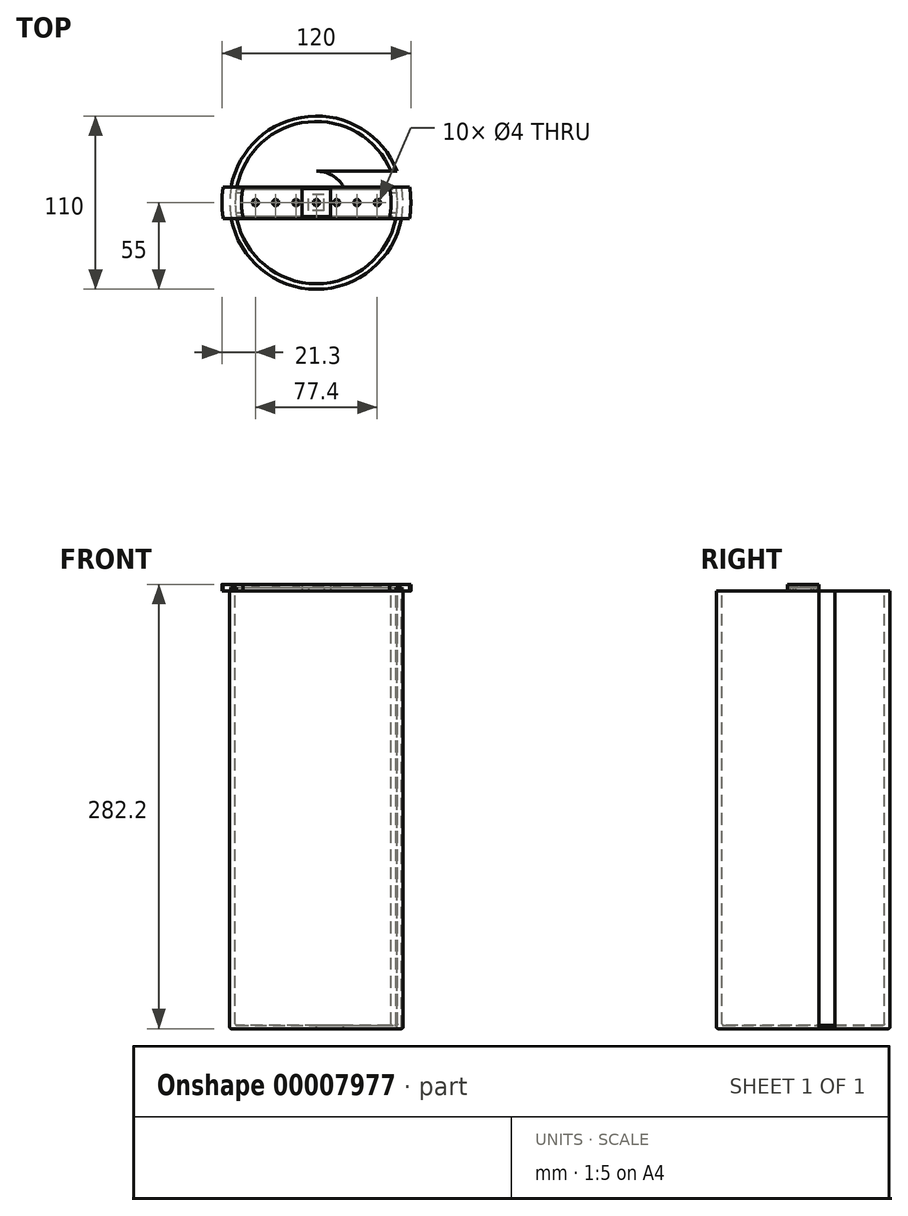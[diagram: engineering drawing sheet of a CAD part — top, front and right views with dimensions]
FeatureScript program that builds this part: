
annotation { "Feature Type Name" : "Feature", "Feature Type Description" : "" }
export const myFeature = defineFeature(function(context is Context, id is Id, definition is map)
    precondition{}
    {
        {
            var Q0;
            Q0=qCreatedBy(makeId("Top.planeOp"),FACE);
            var sketch = newSketch(context, id + "F0", { "sketchPlane" : qUnion([Q0])});
            skCircle(sketch, "E0", {"center": v(0, 0) * mm, "radius": 51.5 * mm});
            skCircle(sketch, "E1", {"center": v(0, 0) * mm, "radius": 4.8 * mm});
            skCircle(sketch, "E2", {"center": v(0, 12.6) * mm, "radius": 4.8 * mm});
            skLineSegment(sketch, "E3", {"start": v(0, 0) * mm, "end": v(0, 33.04) * mm, "construction": true});
            skCircle(sketch, "E4.1.0", {"center": v(-10.91, 6.3) * mm, "radius": 4.8 * mm});
            skCircle(sketch, "E4.2.0", {"center": v(-10.91, -6.3) * mm, "radius": 4.8 * mm});
            skCircle(sketch, "E4.3.0", {"center": v(0, -12.6) * mm, "radius": 4.8 * mm});
            skCircle(sketch, "E4.4.0", {"center": v(10.91, -6.3) * mm, "radius": 4.8 * mm});
            skCircle(sketch, "E4.5.0", {"center": v(10.91, 6.3) * mm, "radius": 4.8 * mm});
            skCircle(sketch, "E5", {"center": v(0, 0) * mm, "radius": 7.8 * mm, "construction": true});
            skCircle(sketch, "E6", {"center": v(0, 0) * mm, "radius": 20 * mm});
            skLineSegment(sketch, "E7.bottom", {"start": v(-65.9, 20) * mm, "end": v(65.9, 20) * mm});
            skLineSegment(sketch, "E7.top", {"start": v(-65.9, -20) * mm, "end": v(65.9, -20) * mm});
            skLineSegment(sketch, "E7.left", {"start": v(-65.9, 20) * mm, "end": v(-65.9, -20) * mm});
            skLineSegment(sketch, "E7.right", {"start": v(65.9, 20) * mm, "end": v(65.9, -20) * mm});
            skLineSegment(sketch, "E8", {"start": v(-65.9, 0) * mm, "end": v(65.9, 0) * mm, "construction": true});
            skCircle(sketch, "E9", {"center": v(0, 0) * mm, "radius": 55 * mm});
            skLineSegment(sketch, "E10", {"start": v(0, 20) * mm, "end": v(0, -20) * mm, "construction": true});
            skCircle(sketch, "E11", {"center": v(0, 0) * mm, "radius": 60 * mm});
            skCircle(sketch, "E12", {"center": v(0, 12.6) * mm, "radius": 1.75 * mm});
            skCircle(sketch, "E13", {"center": v(10.91, 6.3) * mm, "radius": 1.75 * mm});
            skCircle(sketch, "E14", {"center": v(10.91, -6.3) * mm, "radius": 1.75 * mm});
            skCircle(sketch, "E15", {"center": v(0, -12.6) * mm, "radius": 1.75 * mm});
            skCircle(sketch, "E16", {"center": v(-10.91, 6.3) * mm, "radius": 1.75 * mm});
            skCircle(sketch, "E17", {"center": v(-10.91, -6.3) * mm, "radius": 1.75 * mm});
            skCircle(sketch, "E18", {"center": v(0, 0) * mm, "radius": 1.75 * mm});
            skLineSegment(sketch, "E19.bottom", {"start": v(-65.9, -10) * mm, "end": v(-17.32, -10) * mm});
            skLineSegment(sketch, "E19.top", {"start": v(-65.9, 10) * mm, "end": v(-17.32, 10) * mm});
            skLineSegment(sketch, "E19.left", {"start": v(-65.9, -10) * mm, "end": v(-65.9, 10) * mm});
            skLineSegment(sketch, "E19.right", {"start": v(65.9, -10) * mm, "end": v(65.9, 10) * mm});
            skLineSegment(sketch, "E20.trimOffspring", {"start": v(17.32, -10) * mm, "end": v(65.9, -10) * mm});
            skLineSegment(sketch, "E21.trimOffspring", {"start": v(17.32, 10) * mm, "end": v(65.9, 10) * mm});
            skLineSegment(sketch, "E22.bottom", {"start": v(-24, -5) * mm, "end": v(-47.5, -5) * mm});
            skLineSegment(sketch, "E22.top", {"start": v(-24, 5) * mm, "end": v(-47.5, 5) * mm});
            skLineSegment(sketch, "E22.left", {"start": v(-24, -5) * mm, "end": v(-24, 5) * mm});
            skLineSegment(sketch, "E22.right", {"start": v(-47.5, -5) * mm, "end": v(-47.5, 5) * mm});
            skPoint(sketch, "E22.middle", {"position": v(-35.75, 0) * mm});
            skLineSegment(sketch, "E23.MirrorCS", {"start": v(24, 5) * mm, "end": v(47.5, 5) * mm});
            skLineSegment(sketch, "E24.MirrorCS", {"start": v(24, -5) * mm, "end": v(24, 5) * mm});
            skLineSegment(sketch, "E25.MirrorCS", {"start": v(24, -5) * mm, "end": v(47.5, -5) * mm});
            skLineSegment(sketch, "E26.MirrorCS", {"start": v(47.5, -5) * mm, "end": v(47.5, 5) * mm});
            skSolve(sketch);
        }
        {
            var Q0;
            {var subQ0=sQuery(id+"F0.wireOp",EDGE,"E7.bottom");var subQ1=sQuery(id+"F0.wireOp",EDGE,"E0");var subQ2=makeQuery(id+"F0.imprint","INTERSECT",VERTEX,{"disambiguationData":[OD(0.0)],"derivedFrom":[subQ1,subQ0]});Q0=makeQuery(id+"F0.imprint","IMPRINT",FACE,{"disambiguationData":[TD([[makeQuery(id+"F0.imprint","IMPRINT",EDGE,{"disambiguationData":[TD([[subQ2,-1.0]])],"derivedFrom":subQ1}),-1.0]])]});}
            var Q1;
            {var subQ0=sQuery(id+"F0.wireOp",EDGE,"E7.bottom");var subQ1=sQuery(id+"F0.wireOp",EDGE,"E0");var subQ2=makeQuery(id+"F0.imprint","INTERSECT",VERTEX,{"disambiguationData":[OD(1.0)],"derivedFrom":[subQ1,subQ0]});Q1=makeQuery(id+"F0.imprint","IMPRINT",FACE,{"disambiguationData":[TD([[makeQuery(id+"F0.imprint","IMPRINT",EDGE,{"disambiguationData":[TD([[subQ2,-1.0]])],"derivedFrom":subQ1}),-1.0]])]});}
            var Q2;
            {var subQ0=sQuery(id+"F0.wireOp",EDGE,"E19.top");var subQ1=sQuery(id+"F0.wireOp",EDGE,"E0");var subQ2=makeQuery(id+"F0.imprint","INTERSECT",VERTEX,{"derivedFrom":[subQ1,subQ0]});Q2=makeQuery(id+"F0.imprint","IMPRINT",FACE,{"disambiguationData":[TD([[makeQuery(id+"F0.imprint","IMPRINT",EDGE,{"disambiguationData":[TD([[subQ2,-1.0]])],"derivedFrom":subQ1}),-1.0]])]});}
            var Q3;
            {var subQ0=sQuery(id+"F0.wireOp",EDGE,"E19.bottom");var subQ1=sQuery(id+"F0.wireOp",EDGE,"E0");var subQ2=makeQuery(id+"F0.imprint","INTERSECT",VERTEX,{"derivedFrom":[subQ1,subQ0]});Q3=makeQuery(id+"F0.imprint","IMPRINT",FACE,{"disambiguationData":[TD([[makeQuery(id+"F0.imprint","IMPRINT",EDGE,{"disambiguationData":[TD([[subQ2,-1.0]])],"derivedFrom":subQ1}),-1.0]])]});}
            var Q4;
            {var subQ0=sQuery(id+"F0.wireOp",EDGE,"E7.top");var subQ1=sQuery(id+"F0.wireOp",EDGE,"E0");var subQ2=makeQuery(id+"F0.imprint","INTERSECT",VERTEX,{"disambiguationData":[OD(0.0)],"derivedFrom":[subQ1,subQ0]});Q4=makeQuery(id+"F0.imprint","IMPRINT",FACE,{"disambiguationData":[TD([[makeQuery(id+"F0.imprint","IMPRINT",EDGE,{"disambiguationData":[TD([[subQ2,-1.0]])],"derivedFrom":subQ1}),-1.0]])]});}
            var Q5;
            {var subQ0=sQuery(id+"F0.wireOp",EDGE,"E7.top");var subQ1=sQuery(id+"F0.wireOp",EDGE,"E0");var subQ2=makeQuery(id+"F0.imprint","INTERSECT",VERTEX,{"disambiguationData":[OD(1.0)],"derivedFrom":[subQ1,subQ0]});Q5=makeQuery(id+"F0.imprint","IMPRINT",FACE,{"disambiguationData":[TD([[makeQuery(id+"F0.imprint","IMPRINT",EDGE,{"disambiguationData":[TD([[subQ2,-1.0]])],"derivedFrom":subQ1}),-1.0]])]});}
            var Q6;
            {var subQ0=sQuery(id+"F0.wireOp",EDGE,"E21.trimOffspring");var subQ1=sQuery(id+"F0.wireOp",EDGE,"E0");var subQ2=makeQuery(id+"F0.imprint","INTERSECT",VERTEX,{"derivedFrom":[subQ1,subQ0]});Q6=makeQuery(id+"F0.imprint","IMPRINT",FACE,{"disambiguationData":[TD([[makeQuery(id+"F0.imprint","IMPRINT",EDGE,{"disambiguationData":[TD([[subQ2,1.0]])],"derivedFrom":subQ1}),-1.0]])]});}
            var Q7;
            {var subQ0=sQuery(id+"F0.wireOp",EDGE,"E7.bottom");var subQ1=sQuery(id+"F0.wireOp",EDGE,"E0");var subQ2=makeQuery(id+"F0.imprint","INTERSECT",VERTEX,{"disambiguationData":[OD(0.0)],"derivedFrom":[subQ1,subQ0]});Q7=makeQuery(id+"F0.imprint","IMPRINT",FACE,{"disambiguationData":[TD([[makeQuery(id+"F0.imprint","IMPRINT",EDGE,{"disambiguationData":[TD([[subQ2,1.0]])],"derivedFrom":subQ1}),-1.0]])]});}
            var Q8;
            {var subQ0=sQuery(id+"F0.wireOp",EDGE,"E19.top");var subQ1=sQuery(id+"F0.wireOp",EDGE,"E0");var subQ2=makeQuery(id+"F0.imprint","INTERSECT",VERTEX,{"derivedFrom":[subQ1,subQ0]});Q8=makeQuery(id+"F0.imprint","IMPRINT",FACE,{"disambiguationData":[TD([[makeQuery(id+"F0.imprint","IMPRINT",EDGE,{"disambiguationData":[TD([[subQ2,-1.0]])],"derivedFrom":subQ1}),1.0]])]});}
            var Q9;
            Q9=makeQuery(id+"F0.imprint","IMPRINT",FACE,{"disambiguationData":[TD([[makeQuery(id+"F0.imprint","IMPRINT",EDGE,{"derivedFrom":sQuery(id+"F0.wireOp",EDGE,"E4.2.0")}),1.0]])]});
            var Q10;
            {var subQ0=sQuery(id+"F0.wireOp",EDGE,"E7.bottom");var subQ1=sQuery(id+"F0.wireOp",EDGE,"E0");var subQ2=makeQuery(id+"F0.imprint","INTERSECT",VERTEX,{"disambiguationData":[OD(1.0)],"derivedFrom":[subQ1,subQ0]});Q10=makeQuery(id+"F0.imprint","IMPRINT",FACE,{"disambiguationData":[TD([[makeQuery(id+"F0.imprint","IMPRINT",EDGE,{"disambiguationData":[TD([[subQ2,-1.0]])],"derivedFrom":subQ1}),1.0]])]});}
            var Q11;
            {var subQ0=sQuery(id+"F0.wireOp",EDGE,"E7.bottom");var subQ1=sQuery(id+"F0.wireOp",EDGE,"E0");var subQ2=makeQuery(id+"F0.imprint","INTERSECT",VERTEX,{"disambiguationData":[OD(0.0)],"derivedFrom":[subQ1,subQ0]});Q11=makeQuery(id+"F0.imprint","IMPRINT",FACE,{"disambiguationData":[TD([[makeQuery(id+"F0.imprint","IMPRINT",EDGE,{"disambiguationData":[TD([[subQ2,-1.0]])],"derivedFrom":subQ1}),1.0]])]});}
            var Q12;
            {var subQ0=sQuery(id+"F0.wireOp",EDGE,"E19.bottom");var subQ1=sQuery(id+"F0.wireOp",EDGE,"E0");var subQ2=makeQuery(id+"F0.imprint","INTERSECT",VERTEX,{"derivedFrom":[subQ1,subQ0]});Q12=makeQuery(id+"F0.imprint","IMPRINT",FACE,{"disambiguationData":[TD([[makeQuery(id+"F0.imprint","IMPRINT",EDGE,{"disambiguationData":[TD([[subQ2,-1.0]])],"derivedFrom":subQ1}),1.0]])]});}
            var Q13;
            Q13=makeQuery(id+"F0.imprint","IMPRINT",FACE,{"disambiguationData":[TD([[makeQuery(id+"F0.imprint","IMPRINT",EDGE,{"derivedFrom":sQuery(id+"F0.wireOp",EDGE,"E17")}),1.0]])]});
            var Q14;
            {var subQ0=sQuery(id+"F0.wireOp",EDGE,"E7.top");var subQ1=sQuery(id+"F0.wireOp",EDGE,"E0");var subQ2=makeQuery(id+"F0.imprint","INTERSECT",VERTEX,{"disambiguationData":[OD(0.0)],"derivedFrom":[subQ1,subQ0]});Q14=makeQuery(id+"F0.imprint","IMPRINT",FACE,{"disambiguationData":[TD([[makeQuery(id+"F0.imprint","IMPRINT",EDGE,{"disambiguationData":[TD([[subQ2,-1.0]])],"derivedFrom":subQ1}),1.0]])]});}
            var Q15;
            {var subQ0=sQuery(id+"F0.wireOp",EDGE,"E7.bottom");var subQ1=sQuery(id+"F0.wireOp",EDGE,"E0");var subQ2=makeQuery(id+"F0.imprint","INTERSECT",VERTEX,{"disambiguationData":[OD(0.0)],"derivedFrom":[subQ1,subQ0]});Q15=makeQuery(id+"F0.imprint","IMPRINT",FACE,{"disambiguationData":[TD([[makeQuery(id+"F0.imprint","IMPRINT",EDGE,{"disambiguationData":[TD([[subQ2,1.0]])],"derivedFrom":subQ1}),1.0]])]});}
            var Q16;
            {var subQ0=sQuery(id+"F0.wireOp",EDGE,"E21.trimOffspring");var subQ1=sQuery(id+"F0.wireOp",EDGE,"E0");var subQ2=makeQuery(id+"F0.imprint","INTERSECT",VERTEX,{"derivedFrom":[subQ1,subQ0]});Q16=makeQuery(id+"F0.imprint","IMPRINT",FACE,{"disambiguationData":[TD([[makeQuery(id+"F0.imprint","IMPRINT",EDGE,{"disambiguationData":[TD([[subQ2,1.0]])],"derivedFrom":subQ1}),1.0]])]});}
            var Q17;
            {var subQ0=sQuery(id+"F0.wireOp",EDGE,"E7.top");var subQ1=sQuery(id+"F0.wireOp",EDGE,"E0");var subQ2=makeQuery(id+"F0.imprint","INTERSECT",VERTEX,{"disambiguationData":[OD(1.0)],"derivedFrom":[subQ1,subQ0]});Q17=makeQuery(id+"F0.imprint","IMPRINT",FACE,{"disambiguationData":[TD([[makeQuery(id+"F0.imprint","IMPRINT",EDGE,{"disambiguationData":[TD([[subQ2,-1.0]])],"derivedFrom":subQ1}),1.0]])]});}
            var Q18;
            Q18=makeQuery(id+"F0.imprint","IMPRINT",FACE,{"disambiguationData":[TD([[makeQuery(id+"F0.imprint","IMPRINT",EDGE,{"derivedFrom":sQuery(id+"F0.wireOp",EDGE,"E1")}),-1.0]])]});
            var Q19;
            Q19=makeQuery(id+"F0.imprint","IMPRINT",FACE,{"disambiguationData":[TD([[makeQuery(id+"F0.imprint","IMPRINT",EDGE,{"derivedFrom":sQuery(id+"F0.wireOp",EDGE,"E4.1.0")}),1.0]])]});
            var Q20;
            Q20=makeQuery(id+"F0.imprint","IMPRINT",FACE,{"disambiguationData":[TD([[makeQuery(id+"F0.imprint","IMPRINT",EDGE,{"derivedFrom":sQuery(id+"F0.wireOp",EDGE,"E2")}),1.0]])]});
            var Q21;
            Q21=makeQuery(id+"F0.imprint","IMPRINT",FACE,{"disambiguationData":[TD([[makeQuery(id+"F0.imprint","IMPRINT",EDGE,{"derivedFrom":sQuery(id+"F0.wireOp",EDGE,"E1")}),1.0]])]});
            var Q22;
            Q22=makeQuery(id+"F0.imprint","IMPRINT",FACE,{"disambiguationData":[TD([[makeQuery(id+"F0.imprint","IMPRINT",EDGE,{"derivedFrom":sQuery(id+"F0.wireOp",EDGE,"E4.5.0")}),1.0]])]});
            var Q23;
            Q23=makeQuery(id+"F0.imprint","IMPRINT",FACE,{"disambiguationData":[TD([[makeQuery(id+"F0.imprint","IMPRINT",EDGE,{"derivedFrom":sQuery(id+"F0.wireOp",EDGE,"E4.4.0")}),1.0]])]});
            var Q24;
            Q24=makeQuery(id+"F0.imprint","IMPRINT",FACE,{"disambiguationData":[TD([[makeQuery(id+"F0.imprint","IMPRINT",EDGE,{"derivedFrom":sQuery(id+"F0.wireOp",EDGE,"E4.3.0")}),1.0]])]});
            var Q25;
            Q25=makeQuery(id+"F0.imprint","IMPRINT",FACE,{"disambiguationData":[TD([[makeQuery(id+"F0.imprint","IMPRINT",EDGE,{"derivedFrom":sQuery(id+"F0.wireOp",EDGE,"E16")}),1.0]])]});
            var Q26;
            Q26=makeQuery(id+"F0.imprint","IMPRINT",FACE,{"disambiguationData":[TD([[makeQuery(id+"F0.imprint","IMPRINT",EDGE,{"derivedFrom":sQuery(id+"F0.wireOp",EDGE,"E12")}),1.0]])]});
            var Q27;
            Q27=makeQuery(id+"F0.imprint","IMPRINT",FACE,{"disambiguationData":[TD([[makeQuery(id+"F0.imprint","IMPRINT",EDGE,{"derivedFrom":sQuery(id+"F0.wireOp",EDGE,"E13")}),1.0]])]});
            var Q28;
            Q28=makeQuery(id+"F0.imprint","IMPRINT",FACE,{"disambiguationData":[TD([[makeQuery(id+"F0.imprint","IMPRINT",EDGE,{"derivedFrom":sQuery(id+"F0.wireOp",EDGE,"E14")}),1.0]])]});
            var Q29;
            Q29=makeQuery(id+"F0.imprint","IMPRINT",FACE,{"disambiguationData":[TD([[makeQuery(id+"F0.imprint","IMPRINT",EDGE,{"derivedFrom":sQuery(id+"F0.wireOp",EDGE,"E18")}),1.0]])]});
            var Q30;
            Q30=makeQuery(id+"F0.imprint","IMPRINT",FACE,{"disambiguationData":[TD([[makeQuery(id+"F0.imprint","IMPRINT",EDGE,{"derivedFrom":sQuery(id+"F0.wireOp",EDGE,"E15")}),1.0]])]});
            var Q31;
            Q31=makeQuery(id+"F0.imprint","IMPRINT",FACE,{"disambiguationData":[TD([[makeQuery(id+"F0.imprint","IMPRINT",EDGE,{"derivedFrom":sQuery(id+"F0.wireOp",EDGE,"E22.bottom")}),-1.0]])]});
            var Q32;
            Q32=makeQuery(id+"F0.imprint","IMPRINT",FACE,{"disambiguationData":[TD([[makeQuery(id+"F0.imprint","IMPRINT",EDGE,{"derivedFrom":sQuery(id+"F0.wireOp",EDGE,"E23.MirrorCS")}),-1.0]])]});
            extrude(context, id + "F1", {"entities" : qUnion([Q0, Q1, Q2, Q3, Q4, Q5, Q6, Q7, Q8, Q9, Q10, Q11, Q12, Q13, Q14, Q15, Q16, Q17, Q18, Q19, Q20, Q21, Q22, Q23, Q24, Q25, Q26, Q27, Q28, Q29, Q30, Q31, Q32]), "oppositeDirection" : true, "depth" : 278 * mm});
        }
        {
            var Q0;
            {var subQ0=sQuery(id+"F0.wireOp",EDGE,"E7.bottom");var subQ1=sQuery(id+"F0.wireOp",EDGE,"E0");var subQ2=makeQuery(id+"F0.imprint","INTERSECT",VERTEX,{"disambiguationData":[OD(0.0)],"derivedFrom":[subQ1,subQ0]});Q0=makeQuery(id+"F0.imprint","IMPRINT",FACE,{"disambiguationData":[TD([[makeQuery(id+"F0.imprint","IMPRINT",EDGE,{"disambiguationData":[TD([[subQ2,-1.0]])],"derivedFrom":subQ1}),1.0]])]});}
            var Q1;
            {var subQ0=sQuery(id+"F0.wireOp",EDGE,"E7.bottom");var subQ1=sQuery(id+"F0.wireOp",EDGE,"E0");var subQ2=makeQuery(id+"F0.imprint","INTERSECT",VERTEX,{"disambiguationData":[OD(0.0)],"derivedFrom":[subQ1,subQ0]});Q1=makeQuery(id+"F0.imprint","IMPRINT",FACE,{"disambiguationData":[TD([[makeQuery(id+"F0.imprint","IMPRINT",EDGE,{"disambiguationData":[TD([[subQ2,1.0]])],"derivedFrom":subQ1}),1.0]])]});}
            var Q2;
            {var subQ0=sQuery(id+"F0.wireOp",EDGE,"E21.trimOffspring");var subQ1=sQuery(id+"F0.wireOp",EDGE,"E0");var subQ2=makeQuery(id+"F0.imprint","INTERSECT",VERTEX,{"derivedFrom":[subQ1,subQ0]});Q2=makeQuery(id+"F0.imprint","IMPRINT",FACE,{"disambiguationData":[TD([[makeQuery(id+"F0.imprint","IMPRINT",EDGE,{"disambiguationData":[TD([[subQ2,1.0]])],"derivedFrom":subQ1}),1.0]])]});}
            var Q3;
            {var subQ0=sQuery(id+"F0.wireOp",EDGE,"E7.top");var subQ1=sQuery(id+"F0.wireOp",EDGE,"E0");var subQ2=makeQuery(id+"F0.imprint","INTERSECT",VERTEX,{"disambiguationData":[OD(1.0)],"derivedFrom":[subQ1,subQ0]});Q3=makeQuery(id+"F0.imprint","IMPRINT",FACE,{"disambiguationData":[TD([[makeQuery(id+"F0.imprint","IMPRINT",EDGE,{"disambiguationData":[TD([[subQ2,-1.0]])],"derivedFrom":subQ1}),1.0]])]});}
            var Q4;
            {var subQ0=sQuery(id+"F0.wireOp",EDGE,"E7.top");var subQ1=sQuery(id+"F0.wireOp",EDGE,"E0");var subQ2=makeQuery(id+"F0.imprint","INTERSECT",VERTEX,{"disambiguationData":[OD(0.0)],"derivedFrom":[subQ1,subQ0]});Q4=makeQuery(id+"F0.imprint","IMPRINT",FACE,{"disambiguationData":[TD([[makeQuery(id+"F0.imprint","IMPRINT",EDGE,{"disambiguationData":[TD([[subQ2,-1.0]])],"derivedFrom":subQ1}),1.0]])]});}
            var Q5;
            {var subQ0=sQuery(id+"F0.wireOp",EDGE,"E19.bottom");var subQ1=sQuery(id+"F0.wireOp",EDGE,"E0");var subQ2=makeQuery(id+"F0.imprint","INTERSECT",VERTEX,{"derivedFrom":[subQ1,subQ0]});Q5=makeQuery(id+"F0.imprint","IMPRINT",FACE,{"disambiguationData":[TD([[makeQuery(id+"F0.imprint","IMPRINT",EDGE,{"disambiguationData":[TD([[subQ2,-1.0]])],"derivedFrom":subQ1}),1.0]])]});}
            var Q6;
            {var subQ0=sQuery(id+"F0.wireOp",EDGE,"E7.bottom");var subQ1=sQuery(id+"F0.wireOp",EDGE,"E0");var subQ2=makeQuery(id+"F0.imprint","INTERSECT",VERTEX,{"disambiguationData":[OD(1.0)],"derivedFrom":[subQ1,subQ0]});Q6=makeQuery(id+"F0.imprint","IMPRINT",FACE,{"disambiguationData":[TD([[makeQuery(id+"F0.imprint","IMPRINT",EDGE,{"disambiguationData":[TD([[subQ2,-1.0]])],"derivedFrom":subQ1}),1.0]])]});}
            var Q7;
            {var subQ0=sQuery(id+"F0.wireOp",EDGE,"E19.top");var subQ1=sQuery(id+"F0.wireOp",EDGE,"E0");var subQ2=makeQuery(id+"F0.imprint","INTERSECT",VERTEX,{"derivedFrom":[subQ1,subQ0]});Q7=makeQuery(id+"F0.imprint","IMPRINT",FACE,{"disambiguationData":[TD([[makeQuery(id+"F0.imprint","IMPRINT",EDGE,{"disambiguationData":[TD([[subQ2,-1.0]])],"derivedFrom":subQ1}),1.0]])]});}
            var Q8;
            Q8=makeQuery(id+"F0.imprint","IMPRINT",FACE,{"disambiguationData":[TD([[makeQuery(id+"F0.imprint","IMPRINT",EDGE,{"derivedFrom":sQuery(id+"F0.wireOp",EDGE,"E1")}),-1.0]])]});
            var Q9;
            Q9=makeQuery(id+"F0.imprint","IMPRINT",FACE,{"disambiguationData":[TD([[makeQuery(id+"F0.imprint","IMPRINT",EDGE,{"derivedFrom":sQuery(id+"F0.wireOp",EDGE,"E4.4.0")}),1.0]])]});
            var Q10;
            Q10=makeQuery(id+"F0.imprint","IMPRINT",FACE,{"disambiguationData":[TD([[makeQuery(id+"F0.imprint","IMPRINT",EDGE,{"derivedFrom":sQuery(id+"F0.wireOp",EDGE,"E14")}),1.0]])]});
            var Q11;
            Q11=makeQuery(id+"F0.imprint","IMPRINT",FACE,{"disambiguationData":[TD([[makeQuery(id+"F0.imprint","IMPRINT",EDGE,{"derivedFrom":sQuery(id+"F0.wireOp",EDGE,"E13")}),1.0]])]});
            var Q12;
            Q12=makeQuery(id+"F0.imprint","IMPRINT",FACE,{"disambiguationData":[TD([[makeQuery(id+"F0.imprint","IMPRINT",EDGE,{"derivedFrom":sQuery(id+"F0.wireOp",EDGE,"E4.5.0")}),1.0]])]});
            var Q13;
            Q13=makeQuery(id+"F0.imprint","IMPRINT",FACE,{"disambiguationData":[TD([[makeQuery(id+"F0.imprint","IMPRINT",EDGE,{"derivedFrom":sQuery(id+"F0.wireOp",EDGE,"E2")}),1.0]])]});
            var Q14;
            Q14=makeQuery(id+"F0.imprint","IMPRINT",FACE,{"disambiguationData":[TD([[makeQuery(id+"F0.imprint","IMPRINT",EDGE,{"derivedFrom":sQuery(id+"F0.wireOp",EDGE,"E12")}),1.0]])]});
            var Q15;
            Q15=makeQuery(id+"F0.imprint","IMPRINT",FACE,{"disambiguationData":[TD([[makeQuery(id+"F0.imprint","IMPRINT",EDGE,{"derivedFrom":sQuery(id+"F0.wireOp",EDGE,"E4.1.0")}),1.0]])]});
            var Q16;
            Q16=makeQuery(id+"F0.imprint","IMPRINT",FACE,{"disambiguationData":[TD([[makeQuery(id+"F0.imprint","IMPRINT",EDGE,{"derivedFrom":sQuery(id+"F0.wireOp",EDGE,"E16")}),1.0]])]});
            var Q17;
            Q17=makeQuery(id+"F0.imprint","IMPRINT",FACE,{"disambiguationData":[TD([[makeQuery(id+"F0.imprint","IMPRINT",EDGE,{"derivedFrom":sQuery(id+"F0.wireOp",EDGE,"E4.2.0")}),1.0]])]});
            var Q18;
            Q18=makeQuery(id+"F0.imprint","IMPRINT",FACE,{"disambiguationData":[TD([[makeQuery(id+"F0.imprint","IMPRINT",EDGE,{"derivedFrom":sQuery(id+"F0.wireOp",EDGE,"E17")}),1.0]])]});
            var Q19;
            Q19=makeQuery(id+"F0.imprint","IMPRINT",FACE,{"disambiguationData":[TD([[makeQuery(id+"F0.imprint","IMPRINT",EDGE,{"derivedFrom":sQuery(id+"F0.wireOp",EDGE,"E4.3.0")}),1.0]])]});
            var Q20;
            Q20=makeQuery(id+"F0.imprint","IMPRINT",FACE,{"disambiguationData":[TD([[makeQuery(id+"F0.imprint","IMPRINT",EDGE,{"derivedFrom":sQuery(id+"F0.wireOp",EDGE,"E15")}),1.0]])]});
            var Q21;
            Q21=makeQuery(id+"F0.imprint","IMPRINT",FACE,{"disambiguationData":[TD([[makeQuery(id+"F0.imprint","IMPRINT",EDGE,{"derivedFrom":sQuery(id+"F0.wireOp",EDGE,"E1")}),1.0]])]});
            var Q22;
            Q22=makeQuery(id+"F0.imprint","IMPRINT",FACE,{"disambiguationData":[TD([[makeQuery(id+"F0.imprint","IMPRINT",EDGE,{"derivedFrom":sQuery(id+"F0.wireOp",EDGE,"E18")}),1.0]])]});
            var Q23;
            Q23=makeQuery(id+"F0.imprint","IMPRINT",FACE,{"disambiguationData":[TD([[makeQuery(id+"F0.imprint","IMPRINT",EDGE,{"derivedFrom":sQuery(id+"F0.wireOp",EDGE,"E22.bottom")}),-1.0]])]});
            var Q24;
            Q24=makeQuery(id+"F0.imprint","IMPRINT",FACE,{"disambiguationData":[TD([[makeQuery(id+"F0.imprint","IMPRINT",EDGE,{"derivedFrom":sQuery(id+"F0.wireOp",EDGE,"E23.MirrorCS")}),-1.0]])]});
            extrude(context, id + "F2", {"entities" : qUnion([Q0, Q1, Q2, Q3, Q4, Q5, Q6, Q7, Q8, Q9, Q10, Q11, Q12, Q13, Q14, Q15, Q16, Q17, Q18, Q19, Q20, Q21, Q22, Q23, Q24]), "operationType" : NewBodyOperationType.REMOVE, "oppositeDirection" : true, "depth" : 276 * mm});
        }
        {
            var Q0;
            Q0=makeQuery(id+"F2.boolean.opBoolean","COPY",EDGE,{"derivedFrom":makeQuery(id+"F2.opExtrude","CAP_EDGE",EDGE,{"disambiguationData":[OSD([sQuery(id+"F0.wireOp",EDGE,"E0")])],"isStart":false})});
            var Q1;
            Q1=makeQuery(id+"F1.opExtrude","CAP_EDGE",EDGE,{"disambiguationData":[OSD([sQuery(id+"F0.wireOp",EDGE,"E9")])],"isStart":false});
            fillet(context, id + "F3", {"entities" : qUnion([Q0, Q1]), "radius" : 1 * mm, "tangentPropagation" : true, "allowEdgeOverflow" : false});
        }
        {
            var Q0;
            Q0=qCreatedBy(makeId("Top.planeOp"),FACE);
            var sketch = newSketch(context, id + "F4", { "sketchPlane" : qUnion([Q0])});
            skLineSegment(sketch, "E27.0", {"start": v(-59.16, 10) * mm, "end": v(-17.32, 10) * mm});
            skLineSegment(sketch, "E27.1", {"start": v(17.32, 10) * mm, "end": v(59.16, 10) * mm});
            skLineSegment(sketch, "E27.2", {"start": v(17.32, -10) * mm, "end": v(59.16, -10) * mm});
            skLineSegment(sketch, "E27.3", {"start": v(-59.16, -10) * mm, "end": v(-17.32, -10) * mm});
            skCircle(sketch, "E27.4", {"center": v(0, 0) * mm, "radius": 60 * mm});
            skCircle(sketch, "E27.5", {"center": v(0, 0) * mm, "radius": 51.5 * mm});
            skCircle(sketch, "E27.6", {"center": v(0, 0) * mm, "radius": 55 * mm});
            skLineSegment(sketch, "E28.0", {"start": v(0, 0) * mm, "end": v(0, 33.04) * mm, "construction": true});
            skLineSegment(sketch, "E28.1", {"start": v(0, 20) * mm, "end": v(0, -20) * mm, "construction": true});
            skLineSegment(sketch, "E29", {"start": v(-17.32, 10) * mm, "end": v(17.32, 10) * mm});
            skLineSegment(sketch, "E30", {"start": v(-17.32, -10) * mm, "end": v(17.32, -10) * mm});
            skCircle(sketch, "E31", {"center": v(0, 0) * mm, "radius": 47.5 * mm});
            skLineSegment(sketch, "E32.bottom", {"start": v(4.95, -4.95) * mm, "end": v(-4.95, -4.95) * mm});
            skLineSegment(sketch, "E32.top", {"start": v(4.95, 4.95) * mm, "end": v(-4.95, 4.95) * mm});
            skLineSegment(sketch, "E32.left", {"start": v(4.95, -4.95) * mm, "end": v(4.95, 4.95) * mm});
            skLineSegment(sketch, "E32.right", {"start": v(-4.95, -4.95) * mm, "end": v(-4.95, 4.95) * mm});
            skLineSegment(sketch, "E33.1.0.0", {"start": v(17.85, 4.95) * mm, "end": v(7.95, 4.95) * mm});
            skLineSegment(sketch, "E33.1.0.1", {"start": v(17.85, -4.95) * mm, "end": v(17.85, 4.95) * mm});
            skLineSegment(sketch, "E33.1.0.2", {"start": v(17.85, -4.95) * mm, "end": v(7.95, -4.95) * mm});
            skLineSegment(sketch, "E33.1.0.3", {"start": v(7.95, -4.95) * mm, "end": v(7.95, 4.95) * mm});
            skLineSegment(sketch, "E33.2.0.0", {"start": v(30.75, 4.95) * mm, "end": v(20.85, 4.95) * mm});
            skLineSegment(sketch, "E33.2.0.1", {"start": v(30.75, -4.95) * mm, "end": v(30.75, 4.95) * mm});
            skLineSegment(sketch, "E33.2.0.2", {"start": v(30.75, -4.95) * mm, "end": v(20.85, -4.95) * mm});
            skLineSegment(sketch, "E33.2.0.3", {"start": v(20.85, -4.95) * mm, "end": v(20.85, 4.95) * mm});
            skLineSegment(sketch, "E33.3.0.0", {"start": v(43.65, 4.95) * mm, "end": v(33.75, 4.95) * mm});
            skLineSegment(sketch, "E33.3.0.1", {"start": v(43.65, -4.95) * mm, "end": v(43.65, 4.95) * mm});
            skLineSegment(sketch, "E33.3.0.2", {"start": v(43.65, -4.95) * mm, "end": v(33.75, -4.95) * mm});
            skLineSegment(sketch, "E33.3.0.3", {"start": v(33.75, -4.95) * mm, "end": v(33.75, 4.95) * mm});
            skLineSegment(sketch, "E33.direction1", {"start": v(-4.95, 4.95) * mm, "end": v(7.95, 4.95) * mm, "construction": true});
            skLineSegment(sketch, "E34.MirrorCS", {"start": v(-17.85, 4.95) * mm, "end": v(-7.95, 4.95) * mm});
            skLineSegment(sketch, "E35.MirrorCS", {"start": v(-17.85, -4.95) * mm, "end": v(-17.85, 4.95) * mm});
            skLineSegment(sketch, "E36.MirrorCS", {"start": v(-17.85, -4.95) * mm, "end": v(-7.95, -4.95) * mm});
            skLineSegment(sketch, "E37.MirrorCS", {"start": v(-7.95, -4.95) * mm, "end": v(-7.95, 4.95) * mm});
            skLineSegment(sketch, "E38.MirrorCS", {"start": v(-20.85, -4.95) * mm, "end": v(-20.85, 4.95) * mm});
            skLineSegment(sketch, "E39.MirrorCS", {"start": v(-30.75, 4.95) * mm, "end": v(-20.85, 4.95) * mm});
            skLineSegment(sketch, "E40.MirrorCS", {"start": v(-30.75, -4.95) * mm, "end": v(-20.85, -4.95) * mm});
            skLineSegment(sketch, "E41.MirrorCS", {"start": v(-30.75, -4.95) * mm, "end": v(-30.75, 4.95) * mm});
            skLineSegment(sketch, "E42.MirrorCS", {"start": v(-33.75, -4.95) * mm, "end": v(-33.75, 4.95) * mm});
            skLineSegment(sketch, "E43.MirrorCS", {"start": v(-43.65, -4.95) * mm, "end": v(-33.75, -4.95) * mm});
            skLineSegment(sketch, "E44.MirrorCS", {"start": v(-43.65, 4.95) * mm, "end": v(-33.75, 4.95) * mm});
            skLineSegment(sketch, "E45.MirrorCS", {"start": v(-43.65, -4.95) * mm, "end": v(-43.65, 4.95) * mm});
            skCircle(sketch, "E46", {"center": v(0, 0) * mm, "radius": 2 * mm});
            skCircle(sketch, "E47.1.0.0", {"center": v(12.9, 0) * mm, "radius": 2 * mm});
            skCircle(sketch, "E47.2.0.0", {"center": v(25.8, 0) * mm, "radius": 2 * mm});
            skCircle(sketch, "E47.3.0.0", {"center": v(38.7, 0) * mm, "radius": 2 * mm});
            skLineSegment(sketch, "E47.direction1", {"start": v(0, 0) * mm, "end": v(12.9, 0) * mm, "construction": true});
            skCircle(sketch, "E48.MirrorC", {"center": v(-12.9, 0) * mm, "radius": 2 * mm});
            skCircle(sketch, "E49.MirrorC", {"center": v(-25.8, 0) * mm, "radius": 2 * mm});
            skCircle(sketch, "E50.MirrorC", {"center": v(-38.7, 0) * mm, "radius": 2 * mm});
            skSolve(sketch);
        }
        {
            var Q0;
            {var subQ0=sQuery(id+"F4.wireOp",EDGE,"E29");Q0=makeQuery(id+"F4.imprint","IMPRINT",FACE,{"disambiguationData":[TD([[makeQuery(id+"F4.imprint","IMPRINT",EDGE,{"derivedFrom":subQ0}),-1.0]])]});}
            var Q1;
            {var subQ0=sQuery(id+"F4.wireOp",EDGE,"E27.5");var subQ1=sQuery(id+"F4.wireOp",EDGE,"E27.0");var subQ2=makeQuery(id+"F4.imprint","INTERSECT",VERTEX,{"derivedFrom":[subQ1,subQ0]});Q1=makeQuery(id+"F4.imprint","IMPRINT",FACE,{"disambiguationData":[TD([[makeQuery(id+"F4.imprint","IMPRINT",EDGE,{"disambiguationData":[TD([[subQ2,-1.0]])],"derivedFrom":subQ1}),-1.0]])]});}
            var Q2;
            {var subQ0=sQuery(id+"F4.wireOp",EDGE,"E27.4");var subQ1=sQuery(id+"F4.wireOp",EDGE,"E27.0");var subQ2=makeQuery(id+"F4.imprint","INTERSECT",VERTEX,{"derivedFrom":[subQ1,subQ0]});Q2=makeQuery(id+"F4.imprint","IMPRINT",FACE,{"disambiguationData":[TD([[makeQuery(id+"F4.imprint","IMPRINT",EDGE,{"disambiguationData":[TD([[subQ2,-1.0]])],"derivedFrom":subQ1}),-1.0]])]});}
            var Q3;
            {var subQ0=sQuery(id+"F4.wireOp",EDGE,"E27.6");var subQ1=sQuery(id+"F4.wireOp",EDGE,"E27.0");var subQ2=makeQuery(id+"F4.imprint","INTERSECT",VERTEX,{"derivedFrom":[subQ1,subQ0]});Q3=makeQuery(id+"F4.imprint","IMPRINT",FACE,{"disambiguationData":[TD([[makeQuery(id+"F4.imprint","IMPRINT",EDGE,{"disambiguationData":[TD([[subQ2,-1.0]])],"derivedFrom":subQ1}),-1.0]])]});}
            var Q4;
            {var subQ0=sQuery(id+"F4.wireOp",EDGE,"E31");var subQ1=sQuery(id+"F4.wireOp",EDGE,"E27.1");var subQ2=makeQuery(id+"F4.imprint","INTERSECT",VERTEX,{"derivedFrom":[subQ1,subQ0]});Q4=makeQuery(id+"F4.imprint","IMPRINT",FACE,{"disambiguationData":[TD([[makeQuery(id+"F4.imprint","IMPRINT",EDGE,{"disambiguationData":[TD([[subQ2,-1.0]])],"derivedFrom":subQ1}),-1.0]])]});}
            var Q5;
            {var subQ0=sQuery(id+"F4.wireOp",EDGE,"E27.5");var subQ1=sQuery(id+"F4.wireOp",EDGE,"E27.1");var subQ2=makeQuery(id+"F4.imprint","INTERSECT",VERTEX,{"derivedFrom":[subQ1,subQ0]});Q5=makeQuery(id+"F4.imprint","IMPRINT",FACE,{"disambiguationData":[TD([[makeQuery(id+"F4.imprint","IMPRINT",EDGE,{"disambiguationData":[TD([[subQ2,-1.0]])],"derivedFrom":subQ1}),-1.0]])]});}
            var Q6;
            {var subQ0=sQuery(id+"F4.wireOp",EDGE,"E27.4");var subQ1=sQuery(id+"F4.wireOp",EDGE,"E27.1");var subQ2=makeQuery(id+"F4.imprint","INTERSECT",VERTEX,{"derivedFrom":[subQ1,subQ0]});Q6=makeQuery(id+"F4.imprint","IMPRINT",FACE,{"disambiguationData":[TD([[makeQuery(id+"F4.imprint","IMPRINT",EDGE,{"disambiguationData":[TD([[subQ2,1.0]])],"derivedFrom":subQ1}),-1.0]])]});}
            var Q7;
            Q7=makeQuery(id+"F4.imprint","IMPRINT",FACE,{"disambiguationData":[TD([[makeQuery(id+"F4.imprint","IMPRINT",EDGE,{"derivedFrom":sQuery(id+"F4.wireOp",EDGE,"E42.MirrorCS")}),1.0]])]});
            var Q8;
            Q8=makeQuery(id+"F4.imprint","IMPRINT",FACE,{"disambiguationData":[TD([[makeQuery(id+"F4.imprint","IMPRINT",EDGE,{"derivedFrom":sQuery(id+"F4.wireOp",EDGE,"E38.MirrorCS")}),1.0]])]});
            var Q9;
            Q9=makeQuery(id+"F4.imprint","IMPRINT",FACE,{"disambiguationData":[TD([[makeQuery(id+"F4.imprint","IMPRINT",EDGE,{"derivedFrom":sQuery(id+"F4.wireOp",EDGE,"E34.MirrorCS")}),-1.0]])]});
            var Q10;
            Q10=makeQuery(id+"F4.imprint","IMPRINT",FACE,{"disambiguationData":[TD([[makeQuery(id+"F4.imprint","IMPRINT",EDGE,{"derivedFrom":sQuery(id+"F4.wireOp",EDGE,"E32.bottom")}),-1.0]])]});
            var Q11;
            Q11=makeQuery(id+"F4.imprint","IMPRINT",FACE,{"disambiguationData":[TD([[makeQuery(id+"F4.imprint","IMPRINT",EDGE,{"derivedFrom":sQuery(id+"F4.wireOp",EDGE,"E33.1.0.0")}),1.0]])]});
            var Q12;
            Q12=makeQuery(id+"F4.imprint","IMPRINT",FACE,{"disambiguationData":[TD([[makeQuery(id+"F4.imprint","IMPRINT",EDGE,{"derivedFrom":sQuery(id+"F4.wireOp",EDGE,"E33.2.0.0")}),1.0]])]});
            var Q13;
            Q13=makeQuery(id+"F4.imprint","IMPRINT",FACE,{"disambiguationData":[TD([[makeQuery(id+"F4.imprint","IMPRINT",EDGE,{"derivedFrom":sQuery(id+"F4.wireOp",EDGE,"E33.3.0.0")}),1.0]])]});
            extrude(context, id + "F5", {"entities" : qUnion([Q0, Q1, Q2, Q3, Q4, Q5, Q6, Q7, Q8, Q9, Q10, Q11, Q12, Q13]), "depth" : 4.2 * mm});
        }
        {
            var Q0;
            Q0=makeQuery(id+"F4.imprint","IMPRINT",FACE,{"disambiguationData":[TD([[makeQuery(id+"F4.imprint","IMPRINT",EDGE,{"derivedFrom":sQuery(id+"F4.wireOp",EDGE,"8075f1d4-70f9-4dd5-8ec3-b5ab89f9c9bf0.MirrorC")}),1.0]])]});
            var Q1;
            Q1=makeQuery(id+"F4.imprint","IMPRINT",FACE,{"disambiguationData":[TD([[makeQuery(id+"F4.imprint","IMPRINT",EDGE,{"derivedFrom":sQuery(id+"F4.wireOp",EDGE,"205f96f4-c8fc-4229-a65b-f430040cf765.2.0.0")}),-1.0]])]});
            var Q2;
            Q2=makeQuery(id+"F4.imprint","IMPRINT",FACE,{"disambiguationData":[TD([[makeQuery(id+"F4.imprint","IMPRINT",EDGE,{"derivedFrom":sQuery(id+"F4.wireOp",EDGE,"8d914cb3-9dea-42ac-bea7-a907530d0bcd.1")}),-1.0]])]});
            var Q3;
            Q3=makeQuery(id+"F4.imprint","IMPRINT",FACE,{"disambiguationData":[TD([[makeQuery(id+"F4.imprint","IMPRINT",EDGE,{"derivedFrom":sQuery(id+"F4.wireOp",EDGE,"04902287-73d8-48a6-80b9-1e851868ecae0.MirrorC")}),-1.0]])]});
            var Q4;
            Q4=makeQuery(id+"F4.imprint","IMPRINT",FACE,{"disambiguationData":[TD([[makeQuery(id+"F4.imprint","IMPRINT",EDGE,{"derivedFrom":sQuery(id+"F4.wireOp",EDGE,"8075f1d4-70f9-4dd5-8ec3-b5ab89f9c9bf0.MirrorC")}),-1.0]])]});
            var Q5;
            Q5=makeQuery(id+"F4.imprint","IMPRINT",FACE,{"disambiguationData":[TD([[makeQuery(id+"F4.imprint","IMPRINT",EDGE,{"derivedFrom":sQuery(id+"F4.wireOp",EDGE,"de049f4f-b769-4421-8bf6-e8ee1ef1f7560.MirrorC")}),-1.0]])]});
            var Q6;
            Q6=makeQuery(id+"F4.imprint","IMPRINT",FACE,{"disambiguationData":[TD([[makeQuery(id+"F4.imprint","IMPRINT",EDGE,{"derivedFrom":sQuery(id+"F4.wireOp",EDGE,"205f96f4-c8fc-4229-a65b-f430040cf765.1.0.0")}),1.0]])]});
            var Q7;
            Q7=makeQuery(id+"F4.imprint","IMPRINT",FACE,{"disambiguationData":[TD([[makeQuery(id+"F4.imprint","IMPRINT",EDGE,{"derivedFrom":sQuery(id+"F4.wireOp",EDGE,"205f96f4-c8fc-4229-a65b-f430040cf765.2.0.0")}),1.0]])]});
            var Q8;
            Q8=makeQuery(id+"F4.imprint","IMPRINT",FACE,{"disambiguationData":[TD([[makeQuery(id+"F4.imprint","IMPRINT",EDGE,{"derivedFrom":sQuery(id+"F4.wireOp",EDGE,"205f96f4-c8fc-4229-a65b-f430040cf765.3.0.0")}),1.0]])]});
            var Q9;
            Q9=makeQuery(id+"F4.imprint","IMPRINT",FACE,{"disambiguationData":[TD([[makeQuery(id+"F4.imprint","IMPRINT",EDGE,{"derivedFrom":sQuery(id+"F4.wireOp",EDGE,"8d914cb3-9dea-42ac-bea7-a907530d0bcd.1")}),1.0]])]});
            var Q10;
            {var subQ8=sQuery(id+"F4.wireOp",EDGE,"E29");Q10=makeQuery(id+"F4.imprint","IMPRINT",FACE,{"disambiguationData":[TD([[makeQuery(id+"F4.imprint","IMPRINT",EDGE,{"derivedFrom":subQ8}),-1.0]])]});}
            var Q11;
            Q11=makeQuery(id+"F4.imprint","IMPRINT",FACE,{"disambiguationData":[TD([[makeQuery(id+"F4.imprint","IMPRINT",EDGE,{"derivedFrom":sQuery(id+"F4.wireOp",EDGE,"E42.MirrorCS")}),1.0]])]});
            var Q12;
            Q12=makeQuery(id+"F4.imprint","IMPRINT",FACE,{"disambiguationData":[TD([[makeQuery(id+"F4.imprint","IMPRINT",EDGE,{"derivedFrom":sQuery(id+"F4.wireOp",EDGE,"E38.MirrorCS")}),1.0]])]});
            var Q13;
            Q13=makeQuery(id+"F4.imprint","IMPRINT",FACE,{"disambiguationData":[TD([[makeQuery(id+"F4.imprint","IMPRINT",EDGE,{"derivedFrom":sQuery(id+"F4.wireOp",EDGE,"E34.MirrorCS")}),-1.0]])]});
            var Q14;
            Q14=makeQuery(id+"F4.imprint","IMPRINT",FACE,{"disambiguationData":[TD([[makeQuery(id+"F4.imprint","IMPRINT",EDGE,{"derivedFrom":sQuery(id+"F4.wireOp",EDGE,"E32.bottom")}),-1.0]])]});
            var Q15;
            Q15=makeQuery(id+"F4.imprint","IMPRINT",FACE,{"disambiguationData":[TD([[makeQuery(id+"F4.imprint","IMPRINT",EDGE,{"derivedFrom":sQuery(id+"F4.wireOp",EDGE,"E33.1.0.0")}),1.0]])]});
            var Q16;
            Q16=makeQuery(id+"F4.imprint","IMPRINT",FACE,{"disambiguationData":[TD([[makeQuery(id+"F4.imprint","IMPRINT",EDGE,{"derivedFrom":sQuery(id+"F4.wireOp",EDGE,"E33.2.0.0")}),1.0]])]});
            var Q17;
            Q17=makeQuery(id+"F4.imprint","IMPRINT",FACE,{"disambiguationData":[TD([[makeQuery(id+"F4.imprint","IMPRINT",EDGE,{"derivedFrom":sQuery(id+"F4.wireOp",EDGE,"E33.3.0.0")}),1.0]])]});
            var Q18;
            Q18=makeQuery(id+"F4.imprint","IMPRINT",FACE,{"disambiguationData":[TD([[makeQuery(id+"F4.imprint","IMPRINT",EDGE,{"derivedFrom":sQuery(id+"F4.wireOp",EDGE,"E49.MirrorC")}),-1.0]])]});
            var Q19;
            Q19=makeQuery(id+"F4.imprint","IMPRINT",FACE,{"disambiguationData":[TD([[makeQuery(id+"F4.imprint","IMPRINT",EDGE,{"derivedFrom":sQuery(id+"F4.wireOp",EDGE,"E50.MirrorC")}),-1.0]])]});
            var Q20;
            Q20=makeQuery(id+"F4.imprint","IMPRINT",FACE,{"disambiguationData":[TD([[makeQuery(id+"F4.imprint","IMPRINT",EDGE,{"derivedFrom":sQuery(id+"F4.wireOp",EDGE,"E48.MirrorC")}),-1.0]])]});
            var Q21;
            Q21=makeQuery(id+"F4.imprint","IMPRINT",FACE,{"disambiguationData":[TD([[makeQuery(id+"F4.imprint","IMPRINT",EDGE,{"derivedFrom":sQuery(id+"F4.wireOp",EDGE,"E46")}),1.0]])]});
            var Q22;
            Q22=makeQuery(id+"F4.imprint","IMPRINT",FACE,{"disambiguationData":[TD([[makeQuery(id+"F4.imprint","IMPRINT",EDGE,{"derivedFrom":sQuery(id+"F4.wireOp",EDGE,"E47.1.0.0")}),1.0]])]});
            var Q23;
            Q23=makeQuery(id+"F4.imprint","IMPRINT",FACE,{"disambiguationData":[TD([[makeQuery(id+"F4.imprint","IMPRINT",EDGE,{"derivedFrom":sQuery(id+"F4.wireOp",EDGE,"E47.2.0.0")}),1.0]])]});
            var Q24;
            Q24=makeQuery(id+"F4.imprint","IMPRINT",FACE,{"disambiguationData":[TD([[makeQuery(id+"F4.imprint","IMPRINT",EDGE,{"derivedFrom":sQuery(id+"F4.wireOp",EDGE,"E47.3.0.0")}),1.0]])]});
            extrude(context, id + "F6", {"entities" : qUnion([Q0, Q1, Q2, Q3, Q4, Q5, Q6, Q7, Q8, Q9, Q10, Q11, Q12, Q13, Q14, Q15, Q16, Q17, Q18, Q19, Q20, Q21, Q22, Q23, Q24]), "depth" : 4.2 * mm});
        }
        {
            var Q0;
            Q0=qCreatedBy(makeId("Top.planeOp"),FACE);
            var sketch = newSketch(context, id + "F7", { "sketchPlane" : qUnion([Q0])});
            skLineSegment(sketch, "E51.0", {"start": v(-59.16, 10) * mm, "end": v(-17.32, 10) * mm});
            skLineSegment(sketch, "E51.1", {"start": v(-17.32, 10) * mm, "end": v(17.32, 10) * mm});
            skLineSegment(sketch, "E51.2", {"start": v(17.32, 10) * mm, "end": v(59.16, 10) * mm});
            skLineSegment(sketch, "E51.3", {"start": v(17.32, -10) * mm, "end": v(59.16, -10) * mm});
            skLineSegment(sketch, "E51.4", {"start": v(-17.32, -10) * mm, "end": v(17.32, -10) * mm});
            skLineSegment(sketch, "E51.5", {"start": v(-59.16, -10) * mm, "end": v(-17.32, -10) * mm});
            skLineSegment(sketch, "E52.0.0", {"start": v(-43.65, -4.95) * mm, "end": v(-33.75, -4.95) * mm});
            skLineSegment(sketch, "E52.0.1", {"start": v(-33.75, -4.95) * mm, "end": v(-33.75, 4.95) * mm});
            skLineSegment(sketch, "E52.0.2", {"start": v(-33.75, 4.95) * mm, "end": v(-37.7, 4.95) * mm});
            skLineSegment(sketch, "E52.0.3", {"start": v(-43.65, 4.95) * mm, "end": v(-43.65, -4.95) * mm});
            skLineSegment(sketch, "E53.0.0", {"start": v(-30.75, -4.95) * mm, "end": v(-20.85, -4.95) * mm});
            skLineSegment(sketch, "E53.0.1", {"start": v(-20.85, -4.95) * mm, "end": v(-20.85, 4.95) * mm});
            skLineSegment(sketch, "E53.0.2", {"start": v(-20.85, 4.95) * mm, "end": v(-30.75, 4.95) * mm});
            skLineSegment(sketch, "E53.0.3", {"start": v(-30.75, 4.95) * mm, "end": v(-30.75, -4.95) * mm});
            skLineSegment(sketch, "E53.1.0", {"start": v(-7.95, 4.95) * mm, "end": v(-11.9, 4.95) * mm});
            skLineSegment(sketch, "E53.1.1", {"start": v(-17.85, 4.95) * mm, "end": v(-17.85, -4.95) * mm});
            skLineSegment(sketch, "E53.1.2", {"start": v(-17.85, -4.95) * mm, "end": v(-7.95, -4.95) * mm});
            skLineSegment(sketch, "E53.1.3", {"start": v(-7.95, -4.95) * mm, "end": v(-7.95, 4.95) * mm});
            skLineSegment(sketch, "E53.2.0", {"start": v(-4.95, -4.95) * mm, "end": v(4.95, -4.95) * mm});
            skLineSegment(sketch, "E53.2.1", {"start": v(4.95, -4.95) * mm, "end": v(4.95, 4.95) * mm});
            skLineSegment(sketch, "E53.2.2", {"start": v(4.95, 4.95) * mm, "end": v(-4.95, 4.95) * mm});
            skLineSegment(sketch, "E53.2.3", {"start": v(-4.95, 4.95) * mm, "end": v(-4.95, -4.95) * mm});
            skLineSegment(sketch, "E53.3.0", {"start": v(17.85, -4.95) * mm, "end": v(17.85, 4.95) * mm});
            skLineSegment(sketch, "E53.3.1", {"start": v(17.85, 4.95) * mm, "end": v(7.95, 4.95) * mm});
            skLineSegment(sketch, "E53.3.2", {"start": v(7.95, 4.95) * mm, "end": v(7.95, -4.95) * mm});
            skLineSegment(sketch, "E53.3.3", {"start": v(7.95, -4.95) * mm, "end": v(17.85, -4.95) * mm});
            skLineSegment(sketch, "E53.4.0", {"start": v(30.75, -4.95) * mm, "end": v(30.75, 4.95) * mm});
            skLineSegment(sketch, "E53.4.1", {"start": v(30.75, 4.95) * mm, "end": v(20.85, 4.95) * mm});
            skLineSegment(sketch, "E53.4.2", {"start": v(20.85, 4.95) * mm, "end": v(20.85, -4.95) * mm});
            skLineSegment(sketch, "E53.4.3", {"start": v(20.85, -4.95) * mm, "end": v(30.75, -4.95) * mm});
            skLineSegment(sketch, "E53.5.0", {"start": v(43.65, -4.95) * mm, "end": v(43.65, 4.95) * mm});
            skLineSegment(sketch, "E53.5.1", {"start": v(43.65, 4.95) * mm, "end": v(33.75, 4.95) * mm});
            skLineSegment(sketch, "E53.5.2", {"start": v(33.75, 4.95) * mm, "end": v(33.75, -4.95) * mm});
            skLineSegment(sketch, "E53.5.3", {"start": v(33.75, -4.95) * mm, "end": v(43.65, -4.95) * mm});
            skLineSegment(sketch, "E54", {"start": v(-59.53, 7.5) * mm, "end": v(59.53, 7.5) * mm, "construction": true});
            skLineSegment(sketch, "E55", {"start": v(-12.9, 7.5) * mm, "end": v(-12.9, 4.95) * mm, "construction": true});
            skPoint(sketch, "E55.startSnap0", {"position": v(-12.9, 4.95) * mm});
            skLineSegment(sketch, "E56", {"start": v(12.9, 4.95) * mm, "end": v(12.9, 7.5) * mm, "construction": true});
            skLineSegment(sketch, "E57", {"start": v(38.7, 4.95) * mm, "end": v(38.7, 7.5) * mm, "construction": true});
            skLineSegment(sketch, "E58", {"start": v(-59.53, -7.5) * mm, "end": v(59.53, -7.5) * mm, "construction": true});
            skLineSegment(sketch, "E59", {"start": v(-25.8, -4.95) * mm, "end": v(-25.8, -7.5) * mm, "construction": true});
            skLineSegment(sketch, "E60", {"start": v(0, -4.95) * mm, "end": v(0, -7.5) * mm, "construction": true});
            skLineSegment(sketch, "E61", {"start": v(25.8, -4.95) * mm, "end": v(25.8, -7.5) * mm, "construction": true});
            skCircle(sketch, "E62.0", {"center": v(0, 0) * mm, "radius": 60 * mm});
            skLineSegment(sketch, "E63", {"start": v(-38.7, 4.95) * mm, "end": v(-38.7, 7.5) * mm, "construction": true});
            skLineSegment(sketch, "E64.0", {"start": v(-59.4, 8.5) * mm, "end": v(59.4, 8.5) * mm});
            skLineSegment(sketch, "E65.0", {"start": v(-59.65, 6.5) * mm, "end": v(-39.7, 6.5) * mm});
            skLineSegment(sketch, "E66.0", {"start": v(-37.7, 4.95) * mm, "end": v(-37.7, 6.5) * mm});
            skLineSegment(sketch, "E67.0", {"start": v(-39.7, 4.95) * mm, "end": v(-39.7, 6.5) * mm});
            skLineSegment(sketch, "E68.trimOffspring", {"start": v(-37.7, 6.5) * mm, "end": v(59.65, 6.5) * mm});
            skLineSegment(sketch, "E69.0", {"start": v(-13.9, 6.5) * mm, "end": v(-13.9, 4.95) * mm});
            skLineSegment(sketch, "E70.0", {"start": v(-11.9, 6.5) * mm, "end": v(-11.9, 4.95) * mm});
            skLineSegment(sketch, "E71.trimOffspring", {"start": v(-13.9, 4.95) * mm, "end": v(-17.85, 4.95) * mm});
            skLineSegment(sketch, "E72.trimOffspring", {"start": v(-39.7, 4.95) * mm, "end": v(-43.65, 4.95) * mm});
            skLineSegment(sketch, "E73.0", {"start": v(-59.4, -8.5) * mm, "end": v(59.4, -8.5) * mm});
            skLineSegment(sketch, "E74.0", {"start": v(-59.65, -6.5) * mm, "end": v(59.65, -6.5) * mm});
            skLineSegment(sketch, "E75.0", {"start": v(-26.8, -4.95) * mm, "end": v(-26.8, -7.4) * mm});
            skLineSegment(sketch, "E76.0", {"start": v(-24.8, -4.95) * mm, "end": v(-24.8, -7.4) * mm});
            skLineSegment(sketch, "E77.0", {"start": v(-1, -5.05) * mm, "end": v(-1, -7.5) * mm});
            skLineSegment(sketch, "E78.0", {"start": v(1, -5.05) * mm, "end": v(1, -7.5) * mm});
            skLineSegment(sketch, "E79.0", {"start": v(26.8, -4.95) * mm, "end": v(26.8, -7.4) * mm});
            skLineSegment(sketch, "E80.0", {"start": v(24.8, -4.95) * mm, "end": v(24.8, -7.4) * mm});
            skLineSegment(sketch, "E81.0", {"start": v(13.9, 4.95) * mm, "end": v(13.9, 7.4) * mm});
            skLineSegment(sketch, "E82.0", {"start": v(11.9, 4.95) * mm, "end": v(11.9, 7.4) * mm});
            skLineSegment(sketch, "E83.0", {"start": v(39.7, 4.95) * mm, "end": v(39.7, 7.4) * mm});
            skLineSegment(sketch, "E84.0", {"start": v(37.7, 4.95) * mm, "end": v(37.7, 7.4) * mm});
            skCircle(sketch, "E85.0", {"center": v(0, 0) * mm, "radius": 55 * mm});
            skCircle(sketch, "E85.2", {"center": v(0, 0) * mm, "radius": 51.5 * mm});
            skCircle(sketch, "E85.3", {"center": v(0, 0) * mm, "radius": 47.5 * mm});
            skSolve(sketch);
        }
        {
            var Q0;
            Q0=makeQuery(id+"F4.imprint","IMPRINT",FACE,{"disambiguationData":[TD([[makeQuery(id+"F4.imprint","IMPRINT",EDGE,{"derivedFrom":sQuery(id+"F4.wireOp",EDGE,"04902287-73d8-48a6-80b9-1e851868ecae0.MirrorC")}),-1.0]])]});
            var Q1;
            Q1=makeQuery(id+"F4.imprint","IMPRINT",FACE,{"disambiguationData":[TD([[makeQuery(id+"F4.imprint","IMPRINT",EDGE,{"derivedFrom":sQuery(id+"F4.wireOp",EDGE,"8075f1d4-70f9-4dd5-8ec3-b5ab89f9c9bf0.MirrorC")}),-1.0]])]});
            var Q2;
            Q2=makeQuery(id+"F4.imprint","IMPRINT",FACE,{"disambiguationData":[TD([[makeQuery(id+"F4.imprint","IMPRINT",EDGE,{"derivedFrom":sQuery(id+"F4.wireOp",EDGE,"de049f4f-b769-4421-8bf6-e8ee1ef1f7560.MirrorC")}),-1.0]])]});
            var Q3;
            Q3=makeQuery(id+"F4.imprint","IMPRINT",FACE,{"disambiguationData":[TD([[makeQuery(id+"F4.imprint","IMPRINT",EDGE,{"derivedFrom":sQuery(id+"F4.wireOp",EDGE,"8d914cb3-9dea-42ac-bea7-a907530d0bcd.1")}),1.0]])]});
            var Q4;
            Q4=makeQuery(id+"F4.imprint","IMPRINT",FACE,{"disambiguationData":[TD([[makeQuery(id+"F4.imprint","IMPRINT",EDGE,{"derivedFrom":sQuery(id+"F4.wireOp",EDGE,"205f96f4-c8fc-4229-a65b-f430040cf765.1.0.0")}),1.0]])]});
            var Q5;
            Q5=makeQuery(id+"F4.imprint","IMPRINT",FACE,{"disambiguationData":[TD([[makeQuery(id+"F4.imprint","IMPRINT",EDGE,{"derivedFrom":sQuery(id+"F4.wireOp",EDGE,"205f96f4-c8fc-4229-a65b-f430040cf765.2.0.0")}),1.0]])]});
            var Q6;
            Q6=makeQuery(id+"F4.imprint","IMPRINT",FACE,{"disambiguationData":[TD([[makeQuery(id+"F4.imprint","IMPRINT",EDGE,{"derivedFrom":sQuery(id+"F4.wireOp",EDGE,"205f96f4-c8fc-4229-a65b-f430040cf765.3.0.0")}),1.0]])]});
            var Q7;
            {var subQ0=sQuery(id+"F4.wireOp",EDGE,"E27.6");var subQ1=sQuery(id+"F4.wireOp",EDGE,"E27.0");var subQ2=makeQuery(id+"F4.imprint","INTERSECT",VERTEX,{"derivedFrom":[subQ1,subQ0]});Q7=makeQuery(id+"F4.imprint","IMPRINT",FACE,{"disambiguationData":[TD([[makeQuery(id+"F4.imprint","IMPRINT",EDGE,{"disambiguationData":[TD([[subQ2,-1.0]])],"derivedFrom":subQ1}),-1.0]])]});}
            var Q8;
            {var subQ0=sQuery(id+"F4.wireOp",EDGE,"E27.5");var subQ1=sQuery(id+"F4.wireOp",EDGE,"E27.1");var subQ2=makeQuery(id+"F4.imprint","INTERSECT",VERTEX,{"derivedFrom":[subQ1,subQ0]});Q8=makeQuery(id+"F4.imprint","IMPRINT",FACE,{"disambiguationData":[TD([[makeQuery(id+"F4.imprint","IMPRINT",EDGE,{"disambiguationData":[TD([[subQ2,-1.0]])],"derivedFrom":subQ1}),-1.0]])]});}
            var Q9;
            Q9=makeQuery(id+"F4.imprint","IMPRINT",FACE,{"disambiguationData":[TD([[makeQuery(id+"F4.imprint","IMPRINT",EDGE,{"derivedFrom":sQuery(id+"F4.wireOp",EDGE,"E42.MirrorCS")}),1.0]])]});
            var Q10;
            Q10=makeQuery(id+"F4.imprint","IMPRINT",FACE,{"disambiguationData":[TD([[makeQuery(id+"F4.imprint","IMPRINT",EDGE,{"derivedFrom":sQuery(id+"F4.wireOp",EDGE,"E38.MirrorCS")}),1.0]])]});
            var Q11;
            Q11=makeQuery(id+"F4.imprint","IMPRINT",FACE,{"disambiguationData":[TD([[makeQuery(id+"F4.imprint","IMPRINT",EDGE,{"derivedFrom":sQuery(id+"F4.wireOp",EDGE,"E32.bottom")}),-1.0]])]});
            var Q12;
            Q12=makeQuery(id+"F4.imprint","IMPRINT",FACE,{"disambiguationData":[TD([[makeQuery(id+"F4.imprint","IMPRINT",EDGE,{"derivedFrom":sQuery(id+"F4.wireOp",EDGE,"E33.1.0.0")}),1.0]])]});
            var Q13;
            Q13=makeQuery(id+"F4.imprint","IMPRINT",FACE,{"disambiguationData":[TD([[makeQuery(id+"F4.imprint","IMPRINT",EDGE,{"derivedFrom":sQuery(id+"F4.wireOp",EDGE,"E33.2.0.0")}),1.0]])]});
            var Q14;
            Q14=makeQuery(id+"F4.imprint","IMPRINT",FACE,{"disambiguationData":[TD([[makeQuery(id+"F4.imprint","IMPRINT",EDGE,{"derivedFrom":sQuery(id+"F4.wireOp",EDGE,"E33.3.0.0")}),1.0]])]});
            var Q15;
            Q15=makeQuery(id+"F4.imprint","IMPRINT",FACE,{"disambiguationData":[TD([[makeQuery(id+"F4.imprint","IMPRINT",EDGE,{"derivedFrom":sQuery(id+"F4.wireOp",EDGE,"E34.MirrorCS")}),-1.0]])]});
            var Q16;
            Q16=makeQuery(id+"F4.imprint","IMPRINT",FACE,{"disambiguationData":[TD([[makeQuery(id+"F4.imprint","IMPRINT",EDGE,{"derivedFrom":sQuery(id+"F4.wireOp",EDGE,"E50.MirrorC")}),-1.0]])]});
            var Q17;
            Q17=makeQuery(id+"F4.imprint","IMPRINT",FACE,{"disambiguationData":[TD([[makeQuery(id+"F4.imprint","IMPRINT",EDGE,{"derivedFrom":sQuery(id+"F4.wireOp",EDGE,"E49.MirrorC")}),-1.0]])]});
            var Q18;
            Q18=makeQuery(id+"F4.imprint","IMPRINT",FACE,{"disambiguationData":[TD([[makeQuery(id+"F4.imprint","IMPRINT",EDGE,{"derivedFrom":sQuery(id+"F4.wireOp",EDGE,"E48.MirrorC")}),-1.0]])]});
            var Q19;
            Q19=makeQuery(id+"F4.imprint","IMPRINT",FACE,{"disambiguationData":[TD([[makeQuery(id+"F4.imprint","IMPRINT",EDGE,{"derivedFrom":sQuery(id+"F4.wireOp",EDGE,"E46")}),1.0]])]});
            var Q20;
            Q20=makeQuery(id+"F4.imprint","IMPRINT",FACE,{"disambiguationData":[TD([[makeQuery(id+"F4.imprint","IMPRINT",EDGE,{"derivedFrom":sQuery(id+"F4.wireOp",EDGE,"E47.1.0.0")}),1.0]])]});
            var Q21;
            Q21=makeQuery(id+"F4.imprint","IMPRINT",FACE,{"disambiguationData":[TD([[makeQuery(id+"F4.imprint","IMPRINT",EDGE,{"derivedFrom":sQuery(id+"F4.wireOp",EDGE,"E47.2.0.0")}),1.0]])]});
            var Q22;
            Q22=makeQuery(id+"F4.imprint","IMPRINT",FACE,{"disambiguationData":[TD([[makeQuery(id+"F4.imprint","IMPRINT",EDGE,{"derivedFrom":sQuery(id+"F4.wireOp",EDGE,"E47.3.0.0")}),1.0]])]});
            extrude(context, id + "F8", {"entities" : qUnion([Q0, Q1, Q2, Q3, Q4, Q5, Q6, Q7, Q8, Q9, Q10, Q11, Q12, Q13, Q14, Q15, Q16, Q17, Q18, Q19, Q20, Q21, Q22]), "operationType" : NewBodyOperationType.REMOVE, "depth" : 2.1 * mm});
        }
        {
            var Q0;
            {var subQ0=sQuery(id+"F7.wireOp",EDGE,"E85.0");var subQ1=sQuery(id+"F7.wireOp",EDGE,"E73.0");var subQ2=makeQuery(id+"F7.imprint","INTERSECT",VERTEX,{"disambiguationData":[OD(0.0)],"derivedFrom":[subQ1,subQ0]});Q0=makeQuery(id+"F7.imprint","IMPRINT",FACE,{"disambiguationData":[TD([[makeQuery(id+"F7.imprint","IMPRINT",EDGE,{"disambiguationData":[TD([[subQ2,-1.0]])],"derivedFrom":subQ1}),1.0]])]});}
            var Q1;
            {var subQ0=sQuery(id+"F7.wireOp",EDGE,"E85.2");var subQ1=sQuery(id+"F7.wireOp",EDGE,"E73.0");var subQ2=makeQuery(id+"F7.imprint","INTERSECT",VERTEX,{"disambiguationData":[OD(0.0)],"derivedFrom":[subQ1,subQ0]});Q1=makeQuery(id+"F7.imprint","IMPRINT",FACE,{"disambiguationData":[TD([[makeQuery(id+"F7.imprint","IMPRINT",EDGE,{"disambiguationData":[TD([[subQ2,-1.0]])],"derivedFrom":subQ1}),1.0]])]});}
            var Q2;
            {var subQ0=sQuery(id+"F7.wireOp",EDGE,"E85.3");var subQ1=sQuery(id+"F7.wireOp",EDGE,"E73.0");var subQ2=makeQuery(id+"F7.imprint","INTERSECT",VERTEX,{"disambiguationData":[OD(1.0)],"derivedFrom":[subQ1,subQ0]});Q2=makeQuery(id+"F7.imprint","IMPRINT",FACE,{"disambiguationData":[TD([[makeQuery(id+"F7.imprint","IMPRINT",EDGE,{"disambiguationData":[TD([[subQ2,-1.0]])],"derivedFrom":subQ1}),1.0]])]});}
            var Q3;
            {var subQ0=sQuery(id+"F7.wireOp",EDGE,"E85.2");var subQ1=sQuery(id+"F7.wireOp",EDGE,"E73.0");var subQ2=makeQuery(id+"F7.imprint","INTERSECT",VERTEX,{"disambiguationData":[OD(1.0)],"derivedFrom":[subQ1,subQ0]});Q3=makeQuery(id+"F7.imprint","IMPRINT",FACE,{"disambiguationData":[TD([[makeQuery(id+"F7.imprint","IMPRINT",EDGE,{"disambiguationData":[TD([[subQ2,-1.0]])],"derivedFrom":subQ1}),1.0]])]});}
            var Q4;
            {var subQ0=sQuery(id+"F7.wireOp",EDGE,"E81.0");var subQ1=sQuery(id+"F7.wireOp",EDGE,"E53.3.1");var subQ2=makeQuery(id+"F7.imprint","INTERSECT",VERTEX,{"derivedFrom":[subQ1,subQ0]});Q4=makeQuery(id+"F7.imprint","IMPRINT",FACE,{"disambiguationData":[TD([[makeQuery(id+"F7.imprint","IMPRINT",EDGE,{"disambiguationData":[TD([[subQ2,-1.0]])],"derivedFrom":subQ1}),-1.0]])]});}
            var Q5;
            {var subQ0=sQuery(id+"F7.wireOp",EDGE,"E77.0");var subQ1=sQuery(id+"F7.wireOp",EDGE,"E53.2.0");var subQ2=makeQuery(id+"F7.imprint","INTERSECT",VERTEX,{"derivedFrom":[subQ1,subQ0]});Q5=makeQuery(id+"F7.imprint","IMPRINT",FACE,{"disambiguationData":[TD([[makeQuery(id+"F7.imprint","IMPRINT",EDGE,{"disambiguationData":[TD([[subQ2,-1.0]])],"derivedFrom":subQ1}),-1.0]])]});}
            var Q6;
            {var subQ0=sQuery(id+"F7.wireOp",EDGE,"E79.0");var subQ1=sQuery(id+"F7.wireOp",EDGE,"E53.4.3");var subQ2=makeQuery(id+"F7.imprint","INTERSECT",VERTEX,{"derivedFrom":[subQ1,subQ0]});Q6=makeQuery(id+"F7.imprint","IMPRINT",FACE,{"disambiguationData":[TD([[makeQuery(id+"F7.imprint","IMPRINT",EDGE,{"disambiguationData":[TD([[subQ2,1.0]])],"derivedFrom":subQ1}),-1.0]])]});}
            var Q7;
            {var subQ0=sQuery(id+"F7.wireOp",EDGE,"E75.0");var subQ1=sQuery(id+"F7.wireOp",EDGE,"E53.0.0");var subQ2=makeQuery(id+"F7.imprint","INTERSECT",VERTEX,{"derivedFrom":[subQ1,subQ0]});Q7=makeQuery(id+"F7.imprint","IMPRINT",FACE,{"disambiguationData":[TD([[makeQuery(id+"F7.imprint","IMPRINT",EDGE,{"disambiguationData":[TD([[subQ2,-1.0]])],"derivedFrom":subQ1}),-1.0]])]});}
            var Q8;
            {var subQ0=sQuery(id+"F7.wireOp",EDGE,"E83.0");var subQ1=sQuery(id+"F7.wireOp",EDGE,"E53.5.1");var subQ2=makeQuery(id+"F7.imprint","INTERSECT",VERTEX,{"derivedFrom":[subQ1,subQ0]});Q8=makeQuery(id+"F7.imprint","IMPRINT",FACE,{"disambiguationData":[TD([[makeQuery(id+"F7.imprint","IMPRINT",EDGE,{"disambiguationData":[TD([[subQ2,-1.0]])],"derivedFrom":subQ1}),-1.0]])]});}
            var Q9;
            Q9=makeQuery(id+"F7.imprint","IMPRINT",FACE,{"disambiguationData":[TD([[makeQuery(id+"F7.imprint","IMPRINT",EDGE,{"derivedFrom":sQuery(id+"F7.wireOp",EDGE,"E53.1.0")}),1.0]])]});
            var Q10;
            {var subQ0=sQuery(id+"F7.wireOp",EDGE,"E53.2.1");Q10=makeQuery(id+"F7.imprint","IMPRINT",FACE,{"disambiguationData":[TD([[makeQuery(id+"F7.imprint","IMPRINT",EDGE,{"derivedFrom":subQ0}),1.0]])]});}
            var Q11;
            {var subQ3=sQuery(id+"F7.wireOp",EDGE,"E53.3.0");Q11=makeQuery(id+"F7.imprint","IMPRINT",FACE,{"disambiguationData":[TD([[makeQuery(id+"F7.imprint","IMPRINT",EDGE,{"derivedFrom":subQ3}),1.0]])]});}
            var Q12;
            {var subQ3=sQuery(id+"F7.wireOp",EDGE,"E53.4.0");Q12=makeQuery(id+"F7.imprint","IMPRINT",FACE,{"disambiguationData":[TD([[makeQuery(id+"F7.imprint","IMPRINT",EDGE,{"derivedFrom":subQ3}),1.0]])]});}
            var Q13;
            {var subQ0=sQuery(id+"F7.wireOp",EDGE,"E53.0.1");Q13=makeQuery(id+"F7.imprint","IMPRINT",FACE,{"disambiguationData":[TD([[makeQuery(id+"F7.imprint","IMPRINT",EDGE,{"derivedFrom":subQ0}),1.0]])]});}
            var Q14;
            {var subQ3=sQuery(id+"F7.wireOp",EDGE,"E53.5.0");Q14=makeQuery(id+"F7.imprint","IMPRINT",FACE,{"disambiguationData":[TD([[makeQuery(id+"F7.imprint","IMPRINT",EDGE,{"derivedFrom":subQ3}),1.0]])]});}
            var Q15;
            {var subQ0=sQuery(id+"F4.wireOp",EDGE,"E27.5");var subQ1=sQuery(id+"F4.wireOp",EDGE,"E27.1");var subQ2=makeQuery(id+"F4.imprint","INTERSECT",VERTEX,{"derivedFrom":[subQ1,subQ0]});Q15=makeQuery(id+"F4.imprint","IMPRINT",FACE,{"disambiguationData":[TD([[makeQuery(id+"F4.imprint","IMPRINT",EDGE,{"disambiguationData":[TD([[subQ2,-1.0]])],"derivedFrom":subQ1}),-1.0]])]});}
            var Q16;
            Q16=makeQuery(id+"F7.imprint","IMPRINT",FACE,{"disambiguationData":[TD([[makeQuery(id+"F7.imprint","IMPRINT",EDGE,{"derivedFrom":sQuery(id+"F7.wireOp",EDGE,"E52.0.0")}),1.0]])]});
            var Q17;
            {var subQ0=sQuery(id+"F4.wireOp",EDGE,"E27.6");var subQ1=sQuery(id+"F4.wireOp",EDGE,"E27.0");var subQ2=makeQuery(id+"F4.imprint","INTERSECT",VERTEX,{"derivedFrom":[subQ1,subQ0]});Q17=makeQuery(id+"F4.imprint","IMPRINT",FACE,{"disambiguationData":[TD([[makeQuery(id+"F4.imprint","IMPRINT",EDGE,{"disambiguationData":[TD([[subQ2,-1.0]])],"derivedFrom":subQ1}),-1.0]])]});}
            var Q18;
            {var subQ5=sQuery(id+"F7.wireOp",EDGE,"E85.3");var subQ8=sQuery(id+"F7.wireOp",EDGE,"E73.0");var subQ9=makeQuery(id+"F7.imprint","INTERSECT",VERTEX,{"disambiguationData":[OD(0.0)],"derivedFrom":[subQ8,subQ5]});Q18=makeQuery(id+"F7.imprint","IMPRINT",FACE,{"disambiguationData":[TD([[makeQuery(id+"F7.imprint","IMPRINT",EDGE,{"disambiguationData":[TD([[subQ9,-1.0]])],"derivedFrom":subQ8}),1.0]])]});}
            var Q19;
            {var subQ0=sQuery(id+"F7.wireOp",EDGE,"E85.2");var subQ1=sQuery(id+"F7.wireOp",EDGE,"E64.0");var subQ2=makeQuery(id+"F7.imprint","INTERSECT",VERTEX,{"disambiguationData":[OD(0.0)],"derivedFrom":[subQ1,subQ0]});Q19=makeQuery(id+"F7.imprint","IMPRINT",FACE,{"disambiguationData":[TD([[makeQuery(id+"F7.imprint","IMPRINT",EDGE,{"disambiguationData":[TD([[subQ2,-1.0]])],"derivedFrom":subQ1}),-1.0]])]});}
            var Q20;
            {var subQ0=sQuery(id+"F7.wireOp",EDGE,"E85.3");var subQ1=sQuery(id+"F7.wireOp",EDGE,"E64.0");var subQ2=makeQuery(id+"F7.imprint","INTERSECT",VERTEX,{"disambiguationData":[OD(1.0)],"derivedFrom":[subQ1,subQ0]});Q20=makeQuery(id+"F7.imprint","IMPRINT",FACE,{"disambiguationData":[TD([[makeQuery(id+"F7.imprint","IMPRINT",EDGE,{"disambiguationData":[TD([[subQ2,-1.0]])],"derivedFrom":subQ1}),-1.0]])]});}
            extrude(context, id + "F9", {"entities" : qUnion([Q0, Q1, Q2, Q3, Q4, Q5, Q6, Q7, Q8, Q9, Q10, Q11, Q12, Q13, Q14, Q15, Q16, Q17, Q18, Q19, Q20]), "operationType" : NewBodyOperationType.REMOVE, "depth" : 2.1 * mm});
        }
        {
            var Q0;
            Q0=qCreatedBy(makeId("Top.planeOp"),FACE);
            var sketch = newSketch(context, id + "F10", { "sketchPlane" : qUnion([Q0])});
            skLineSegment(sketch, "E86.bottom", {"start": v(9, -9) * mm, "end": v(-9, -9) * mm});
            skLineSegment(sketch, "E86.top", {"start": v(9, 9) * mm, "end": v(-9, 9) * mm});
            skLineSegment(sketch, "E86.left", {"start": v(9, -9) * mm, "end": v(9, 9) * mm});
            skLineSegment(sketch, "E86.right", {"start": v(-9, -9) * mm, "end": v(-9, 9) * mm});
            skPoint(sketch, "E86.middle", {"position": v(0, 0) * mm});
            skLineSegment(sketch, "E87.bottom", {"start": v(4.95, -4.95) * mm, "end": v(-4.95, -4.95) * mm});
            skLineSegment(sketch, "E87.top", {"start": v(4.95, 4.95) * mm, "end": v(-4.95, 4.95) * mm});
            skLineSegment(sketch, "E87.left", {"start": v(4.95, -4.95) * mm, "end": v(4.95, 4.95) * mm});
            skLineSegment(sketch, "E87.right", {"start": v(-4.95, -4.95) * mm, "end": v(-4.95, 4.95) * mm});
            skSolve(sketch);
        }
        {
            var Q0;
            Q0=makeQuery(id+"F10.imprint","IMPRINT",FACE,{"disambiguationData":[TD([[makeQuery(id+"F10.imprint","IMPRINT",EDGE,{"derivedFrom":sQuery(id+"F10.wireOp",EDGE,"E86.bottom")}),-1.0]])]});
            var Q1;
            Q1=makeQuery(id+"F10.imprint","IMPRINT",FACE,{"disambiguationData":[TD([[makeQuery(id+"F10.imprint","IMPRINT",EDGE,{"derivedFrom":sQuery(id+"F10.wireOp",EDGE,"E87.bottom")}),-1.0]])]});
            extrude(context, id + "F11", {"entities" : qUnion([Q0, Q1]), "depth" : 4.2 * mm});
        }
        {
            var Q0;
            Q0=makeQuery(id+"F10.imprint","IMPRINT",FACE,{"disambiguationData":[TD([[makeQuery(id+"F10.imprint","IMPRINT",EDGE,{"derivedFrom":sQuery(id+"F10.wireOp",EDGE,"E87.bottom")}),-1.0]])]});
            extrude(context, id + "F12", {"entities" : qUnion([Q0]), "operationType" : NewBodyOperationType.REMOVE, "depth" : 2.1 * mm});
        }
    });
